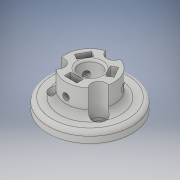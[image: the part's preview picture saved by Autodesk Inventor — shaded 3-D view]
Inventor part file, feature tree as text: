
AUTODESK INVENTOR PART (.ipt)
format: ipt  version: 2019 (Build 230136000, 136)  size: 291,328 bytes
history: native  units: mm
features: sketch x6, extrude x4, fillet x4, hole x2, plane x1, pattern_circular x1
ambient origin geometry x8: Origin, YZ Plane, XZ Plane, XY Plane, X Axis, Y Axis, Z Axis, Center Point
bodies: Solid1 (feature_tree)
feature tree (18):
  extrude  "Extrusion1"  Depth=6.0mm TaperAngle=0.0deg
  extrude  "Extrusion2"  Depth=12.0mm TaperAngle=0.0deg
  hole  "Hole1"  [1 undecoded]
  hole  "Hole2"  [1 undecoded]
  plane  "Work Plane1"
  extrude  "Extrusion3"  Depth=1.0mm TaperAngle=0.0deg
  extrude  "Extrusion4"  Depth=1.0mm
  fillet  "Fillet1"  Radius=3.25mm
  fillet  "Fillet2"  Radius=1.0mm
  pattern_circular  "Circular Pattern1"  [2 undecoded]
  fillet  "Fillet3"  Radius=30.0mm
  fillet  "Fillet4"  Radius=2.0mm
  sketch  "Sketch1"  dims[d0=40.0mm d1=6.0mm d2=0.0mm]
  sketch  "Sketch2"  dims[d3=23.0mm d4=12.0mm d5=0.0mm]
  sketch  "Sketch3"  dims[d6=23.0mm d7=60.0mm d9=360.0deg]
  sketch  "Sketch4"  dims[d11=3.3mm d12=6.0mm d13=7.0mm d14=15.0mm d15=90.0deg d16=8.0mm d17=90.0deg]
  sketch  "Sketch7"  dims[d18=10.25mm d19=6.0mm d20=7.0mm d21=13.0mm d22=90.0deg d23=8.0mm d24=90.0deg d25=7.75mm]
  sketch  "Sketch8"  dims[d27=6.0mm d28=3.0mm d29=0.0mm d30=3.1mm d31=3.25mm d32=4.25mm d33=0.0mm d34=0.0mm d35=1.0mm d36=3.0mm d37=30.0mm d38=360.0deg d40=2.0mm d41=1.0mm]
note: 4 required parameter values undecoded (feature->parameter linkage not recoverable at this tier; creation-order binding heuristic only, values carry confidence <= 0.55)
